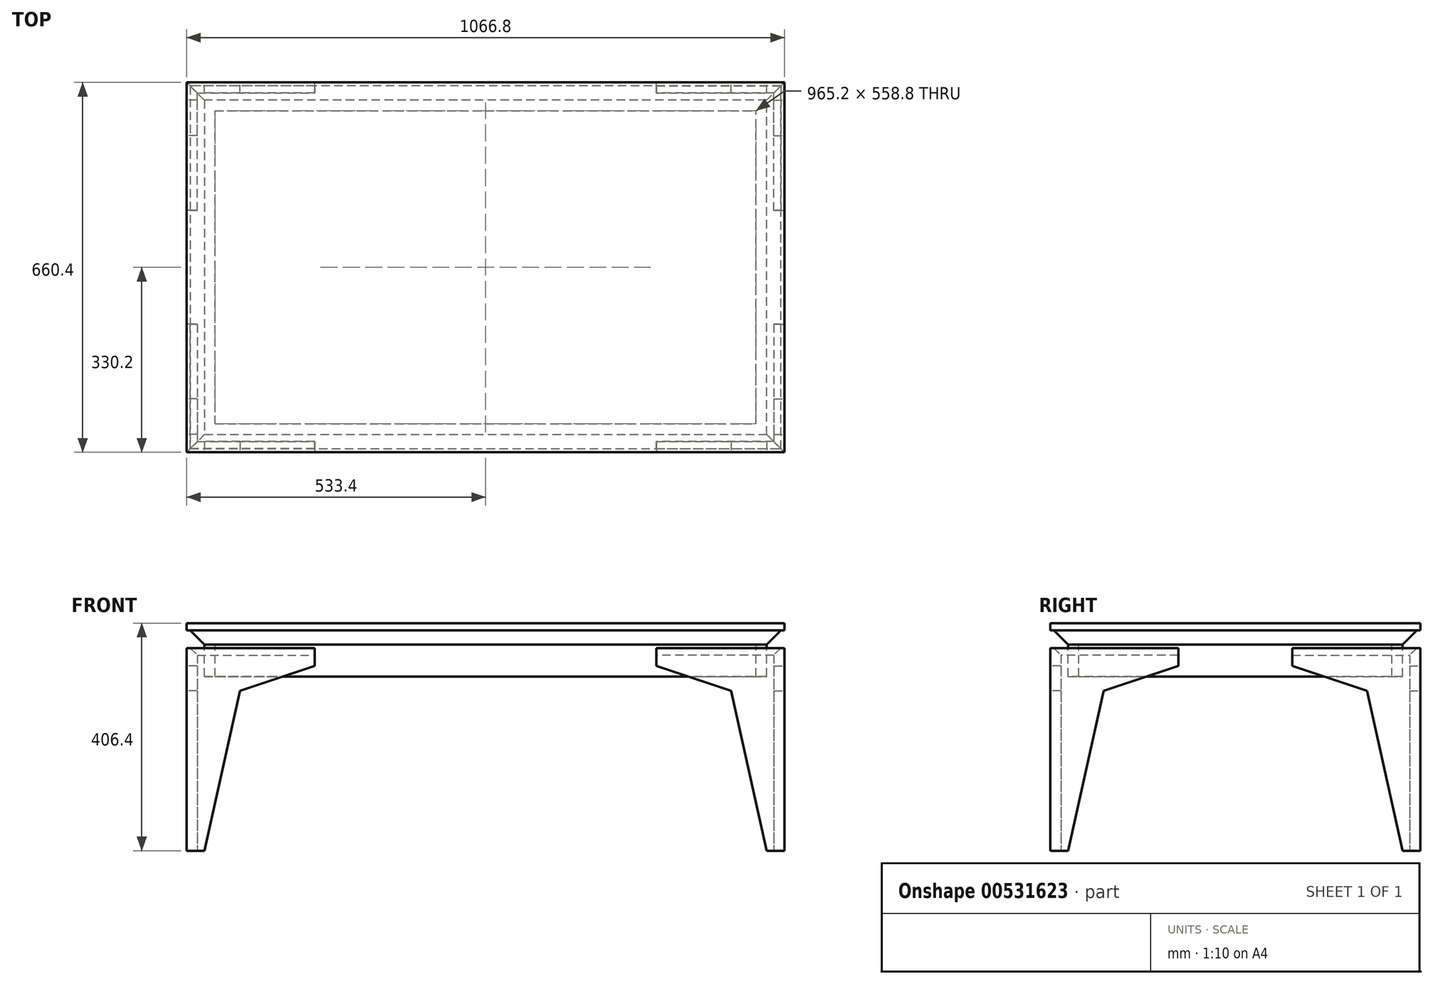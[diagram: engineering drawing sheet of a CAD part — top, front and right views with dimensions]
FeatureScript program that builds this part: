
annotation { "Feature Type Name" : "Feature", "Feature Type Description" : "" }
export const myFeature = defineFeature(function(context is Context, id is Id, definition is map)
    precondition{}
    {
        {
            var Q0;
            Q0=qCreatedBy(makeId("Top.planeOp"),FACE);
            cPlane(context, id + "F0", {"entities" : qUnion([Q0]), "cplaneType" : CPlaneType.OFFSET, "offset" : 406.4 * mm, "width" : 152.4 * mm, "height" : 152.4 * mm});
        }
        {
            var Q0;
            Q0=qCreatedBy(id+"F0.planeOp",FACE);
            var sketch = newSketch(context, id + "F1", { "sketchPlane" : qUnion([Q0])});
            skLineSegment(sketch, "E0.bottom", {"start": v(-533.4, 330.2) * mm, "end": v(533.4, 330.2) * mm});
            skLineSegment(sketch, "E0.top", {"start": v(-533.4, -330.2) * mm, "end": v(533.4, -330.2) * mm});
            skLineSegment(sketch, "E0.left", {"start": v(-533.4, 330.2) * mm, "end": v(-533.4, -330.2) * mm});
            skLineSegment(sketch, "E0.right", {"start": v(533.4, 330.2) * mm, "end": v(533.4, -330.2) * mm});
            skSolve(sketch);
        }
        {
            var Q0;
            Q0=makeQuery(id+"F1.imprint","IMPRINT",FACE,{"disambiguationData":[TD([[makeQuery(id+"F1.imprint","IMPRINT",EDGE,{"derivedFrom":sQuery(id+"F1.wireOp",EDGE,"E0.bottom")}),-1.0]])]});
            extrude(context, id + "F2", {"entities" : qUnion([Q0]), "oppositeDirection" : true, "depth" : 12.7 * mm, "offsetDistance" : 25.4 * mm});
        }
        {
            var Q0;
            Q0=makeQuery(id+"F2.opExtrude","CAP_FACE",FACE,{"disambiguationData":[OSD([sQuery(id+"F1.wireOp",EDGE,"E0.bottom"),sQuery(id+"F1.wireOp",EDGE,"E0.top"),sQuery(id+"F1.wireOp",EDGE,"E0.left"),sQuery(id+"F1.wireOp",EDGE,"E0.right")])],"isStart":false});
            var sketch = newSketch(context, id + "F3", { "sketchPlane" : qUnion([Q0])});
            skLineSegment(sketch, "E1.bottom", {"start": v(-527.05, 323.85) * mm, "end": v(527.05, 323.85) * mm});
            skLineSegment(sketch, "E1.top", {"start": v(-527.05, -323.85) * mm, "end": v(527.05, -323.85) * mm});
            skLineSegment(sketch, "E1.left", {"start": v(-527.05, 323.85) * mm, "end": v(-527.05, -323.85) * mm});
            skLineSegment(sketch, "E1.right", {"start": v(527.05, 323.85) * mm, "end": v(527.05, -323.85) * mm});
            skSolve(sketch);
        }
        {
            var Q0;
            Q0=makeQuery(id+"F3.imprint","IMPRINT",FACE,{"disambiguationData":[TD([[makeQuery(id+"F3.imprint","IMPRINT",EDGE,{"derivedFrom":sQuery(id+"F3.wireOp",EDGE,"E1.bottom")}),-1.0]])]});
            extrude(context, id + "F4", {"entities" : qUnion([Q0]), "operationType" : NewBodyOperationType.ADD, "depth" : 25.4 * mm, "offsetDistance" : 25.4 * mm, "hasDraft" : true, "draftAngle" : 45 * degree, "draftPullDirection" : true});
        }
        {
            var Q0;
            Q0=makeQuery(id+"F2.opExtrude","SWEPT_FACE",FACE,{"disambiguationData":[OSD([sQuery(id+"F1.wireOp",EDGE,"E0.top")])]});
            var sketch = newSketch(context, id + "F5", { "sketchPlane" : qUnion([Q0])});
            skLineSegment(sketch, "E2.bottom", {"start": v(-533.4, 361.95) * mm, "end": v(-304.8, 361.95) * mm});
            skLineSegment(sketch, "E2.top", {"start": v(-533.4, 0) * mm, "end": v(-501.65, 0) * mm});
            skLineSegment(sketch, "E2.left", {"start": v(-533.4, 361.95) * mm, "end": v(-533.4, 0) * mm});
            skLineSegment(sketch, "E2.right", {"start": v(-304.8, 361.95) * mm, "end": v(-304.8, 330.2) * mm});
            skLineSegment(sketch, "E3", {"start": v(-304.8, 330.2) * mm, "end": v(-438.15, 285.75) * mm});
            skLineSegment(sketch, "E4", {"start": v(-438.15, 285.75) * mm, "end": v(-501.65, 0) * mm});
            skSolve(sketch);
        }
        {
            var Q0;
            Q0=makeQuery(id+"F5.imprint","IMPRINT",FACE,{"disambiguationData":[TD([[makeQuery(id+"F5.imprint","IMPRINT",EDGE,{"derivedFrom":sQuery(id+"F5.wireOp",EDGE,"E2.bottom")}),-1.0]])]});
            extrude(context, id + "F6", {"entities" : qUnion([Q0]), "oppositeDirection" : true, "depth" : 19.05 * mm, "offsetDistance" : 25.4 * mm});
        }
        {
            var Q0;
            Q0=makeQuery(id+"F6.opExtrude","CAP_EDGE",EDGE,{"disambiguationData":[OSD([sQuery(id+"F5.wireOp",EDGE,"E2.bottom")])],"isStart":false});
            chamfer(context, id + "F7", {"entities" : qUnion([Q0]), "width" : 12.7 * mm, "tangentPropagation" : true});
        }
        {
            var Q0;
            Q0=makeQuery(id+"F6.opExtrude","CAP_EDGE",EDGE,{"disambiguationData":[OSD([sQuery(id+"F5.wireOp",EDGE,"E2.left")])],"isStart":false});
            chamfer(context, id + "F8", {"entities" : qUnion([Q0]), "width" : 19.05 * mm, "tangentPropagation" : true});
        }
        {
            var Q0;
            Q0=makeQuery(id+"F2.opExtrude","SWEPT_FACE",FACE,{"disambiguationData":[OSD([sQuery(id+"F1.wireOp",EDGE,"E0.left")])]});
            var sketch = newSketch(context, id + "F9", { "sketchPlane" : qUnion([Q0])});
            skLineSegment(sketch, "E5", {"start": v(298.45, 0) * mm, "end": v(330.2, 0) * mm});
            skLineSegment(sketch, "E6", {"start": v(330.2, 0) * mm, "end": v(330.2, 361.95) * mm});
            skLineSegment(sketch, "E7", {"start": v(330.2, 361.95) * mm, "end": v(101.6, 361.95) * mm});
            skLineSegment(sketch, "E8", {"start": v(101.6, 361.95) * mm, "end": v(101.6, 330.2) * mm});
            skLineSegment(sketch, "E9", {"start": v(101.6, 330.2) * mm, "end": v(234.95, 285.75) * mm});
            skLineSegment(sketch, "E10", {"start": v(234.95, 285.75) * mm, "end": v(298.45, 0) * mm});
            skSolve(sketch);
        }
        {
            var Q0;
            Q0=makeQuery(id+"F9.imprint","IMPRINT",FACE,{"disambiguationData":[TD([[makeQuery(id+"F9.imprint","IMPRINT",EDGE,{"derivedFrom":sQuery(id+"F9.wireOp",EDGE,"E5")}),1.0]])]});
            extrude(context, id + "F10", {"entities" : qUnion([Q0]), "oppositeDirection" : true, "depth" : 19.05 * mm, "offsetDistance" : 25.4 * mm});
        }
        {
            var Q0;
            Q0=makeQuery(id+"F10.opExtrude","CAP_EDGE",EDGE,{"disambiguationData":[OSD([sQuery(id+"F9.wireOp",EDGE,"E7")])],"isStart":false});
            chamfer(context, id + "F11", {"entities" : qUnion([Q0]), "width" : 12.7 * mm, "tangentPropagation" : true});
        }
        {
            var Q0;
            Q0=makeQuery(id+"F10.opExtrude","CAP_EDGE",EDGE,{"disambiguationData":[OSD([sQuery(id+"F9.wireOp",EDGE,"E6")])],"isStart":false});
            chamfer(context, id + "F12", {"entities" : qUnion([Q0]), "width" : 19.05 * mm, "tangentPropagation" : true});
        }
        {
            var Q0;
            Q0=makeQuery(id+"F6.opExtrude","SWEPT_BODY",BODY,{"disambiguationData":[OSD([sQuery(id+"F5.wireOp",EDGE,"E2.bottom"),sQuery(id+"F5.wireOp",EDGE,"E2.top"),sQuery(id+"F5.wireOp",EDGE,"E2.left"),sQuery(id+"F5.wireOp",EDGE,"E2.right"),sQuery(id+"F5.wireOp",EDGE,"E3"),sQuery(id+"F5.wireOp",EDGE,"E4")])]});
            var Q1;
            Q1=makeQuery(id+"F10.opExtrude","SWEPT_BODY",BODY,{"disambiguationData":[OSD([sQuery(id+"F9.wireOp",EDGE,"E5"),sQuery(id+"F9.wireOp",EDGE,"E6"),sQuery(id+"F9.wireOp",EDGE,"E7"),sQuery(id+"F9.wireOp",EDGE,"E8"),sQuery(id+"F9.wireOp",EDGE,"E9"),sQuery(id+"F9.wireOp",EDGE,"E10")])]});
            var Q2;
            Q2=qCreatedBy(makeId("Front.planeOp"),FACE);
            mirror(context, id + "F13", {"entities" : qUnion([Q0, Q1]), "mirrorPlane" : qUnion([Q2])});
        }
        {
            var Q0;
            Q0=makeQuery(id+"F6.opExtrude","SWEPT_BODY",BODY,{"disambiguationData":[OSD([sQuery(id+"F5.wireOp",EDGE,"E2.bottom"),sQuery(id+"F5.wireOp",EDGE,"E2.top"),sQuery(id+"F5.wireOp",EDGE,"E2.left"),sQuery(id+"F5.wireOp",EDGE,"E2.right"),sQuery(id+"F5.wireOp",EDGE,"E3"),sQuery(id+"F5.wireOp",EDGE,"E4")])]});
            var Q1;
            Q1=makeQuery(id+"F10.opExtrude","SWEPT_BODY",BODY,{"disambiguationData":[OSD([sQuery(id+"F9.wireOp",EDGE,"E5"),sQuery(id+"F9.wireOp",EDGE,"E6"),sQuery(id+"F9.wireOp",EDGE,"E7"),sQuery(id+"F9.wireOp",EDGE,"E8"),sQuery(id+"F9.wireOp",EDGE,"E9"),sQuery(id+"F9.wireOp",EDGE,"E10")])]});
            var Q2;
            Q2=makeQuery(id+"F13.opPattern","COPY",BODY,{"derivedFrom":makeQuery(id+"F6.opExtrude","SWEPT_BODY",BODY,{"disambiguationData":[OSD([sQuery(id+"F5.wireOp",EDGE,"E2.bottom"),sQuery(id+"F5.wireOp",EDGE,"E2.top"),sQuery(id+"F5.wireOp",EDGE,"E2.left"),sQuery(id+"F5.wireOp",EDGE,"E2.right"),sQuery(id+"F5.wireOp",EDGE,"E3"),sQuery(id+"F5.wireOp",EDGE,"E4")])]}),"instanceName":"1"});
            var Q3;
            Q3=makeQuery(id+"F13.opPattern","COPY",BODY,{"derivedFrom":makeQuery(id+"F10.opExtrude","SWEPT_BODY",BODY,{"disambiguationData":[OSD([sQuery(id+"F9.wireOp",EDGE,"E5"),sQuery(id+"F9.wireOp",EDGE,"E6"),sQuery(id+"F9.wireOp",EDGE,"E7"),sQuery(id+"F9.wireOp",EDGE,"E8"),sQuery(id+"F9.wireOp",EDGE,"E9"),sQuery(id+"F9.wireOp",EDGE,"E10")])]}),"instanceName":"1"});
            var Q4;
            Q4=qCreatedBy(makeId("Right.planeOp"),FACE);
            mirror(context, id + "F14", {"entities" : qUnion([Q0, Q1, Q2, Q3]), "mirrorPlane" : qUnion([Q4])});
        }
        {
            var Q0;
            Q0=makeQuery(id+"F4.opExtrude","CAP_FACE",FACE,{"disambiguationData":[OSD([sQuery(id+"F3.wireOp",EDGE,"E1.bottom"),sQuery(id+"F3.wireOp",EDGE,"E1.top"),sQuery(id+"F3.wireOp",EDGE,"E1.left"),sQuery(id+"F3.wireOp",EDGE,"E1.right")])],"isStart":false});
            var sketch = newSketch(context, id + "F15", { "sketchPlane" : qUnion([Q0])});
            skLineSegment(sketch, "E11.bottom", {"start": v(-501.65, 298.45) * mm, "end": v(501.65, 298.45) * mm});
            skLineSegment(sketch, "E11.top", {"start": v(-501.65, -298.45) * mm, "end": v(501.65, -298.45) * mm});
            skLineSegment(sketch, "E11.left", {"start": v(-501.65, 298.45) * mm, "end": v(-501.65, -298.45) * mm});
            skLineSegment(sketch, "E11.right", {"start": v(501.65, 298.45) * mm, "end": v(501.65, -298.45) * mm});
            skLineSegment(sketch, "E12.bottom", {"start": v(-482.6, 279.4) * mm, "end": v(482.6, 279.4) * mm});
            skLineSegment(sketch, "E12.top", {"start": v(-482.6, -279.4) * mm, "end": v(482.6, -279.4) * mm});
            skLineSegment(sketch, "E12.left", {"start": v(-482.6, 279.4) * mm, "end": v(-482.6, -279.4) * mm});
            skLineSegment(sketch, "E12.right", {"start": v(482.6, 279.4) * mm, "end": v(482.6, -279.4) * mm});
            skLineSegment(sketch, "E13", {"start": v(-501.65, 298.45) * mm, "end": v(-482.6, 279.4) * mm, "construction": true});
            skLineSegment(sketch, "E14", {"start": v(482.6, -279.4) * mm, "end": v(501.65, -298.45) * mm, "construction": true});
            skSolve(sketch);
        }
        {
            var Q0;
            Q0 = qSketchRegion(id + "F15", true);
            extrude(context, id + "F16", {"entities" : qUnion([Q0]), "depth" : 57.15 * mm, "offsetDistance" : 25.4 * mm});
        }
    });
